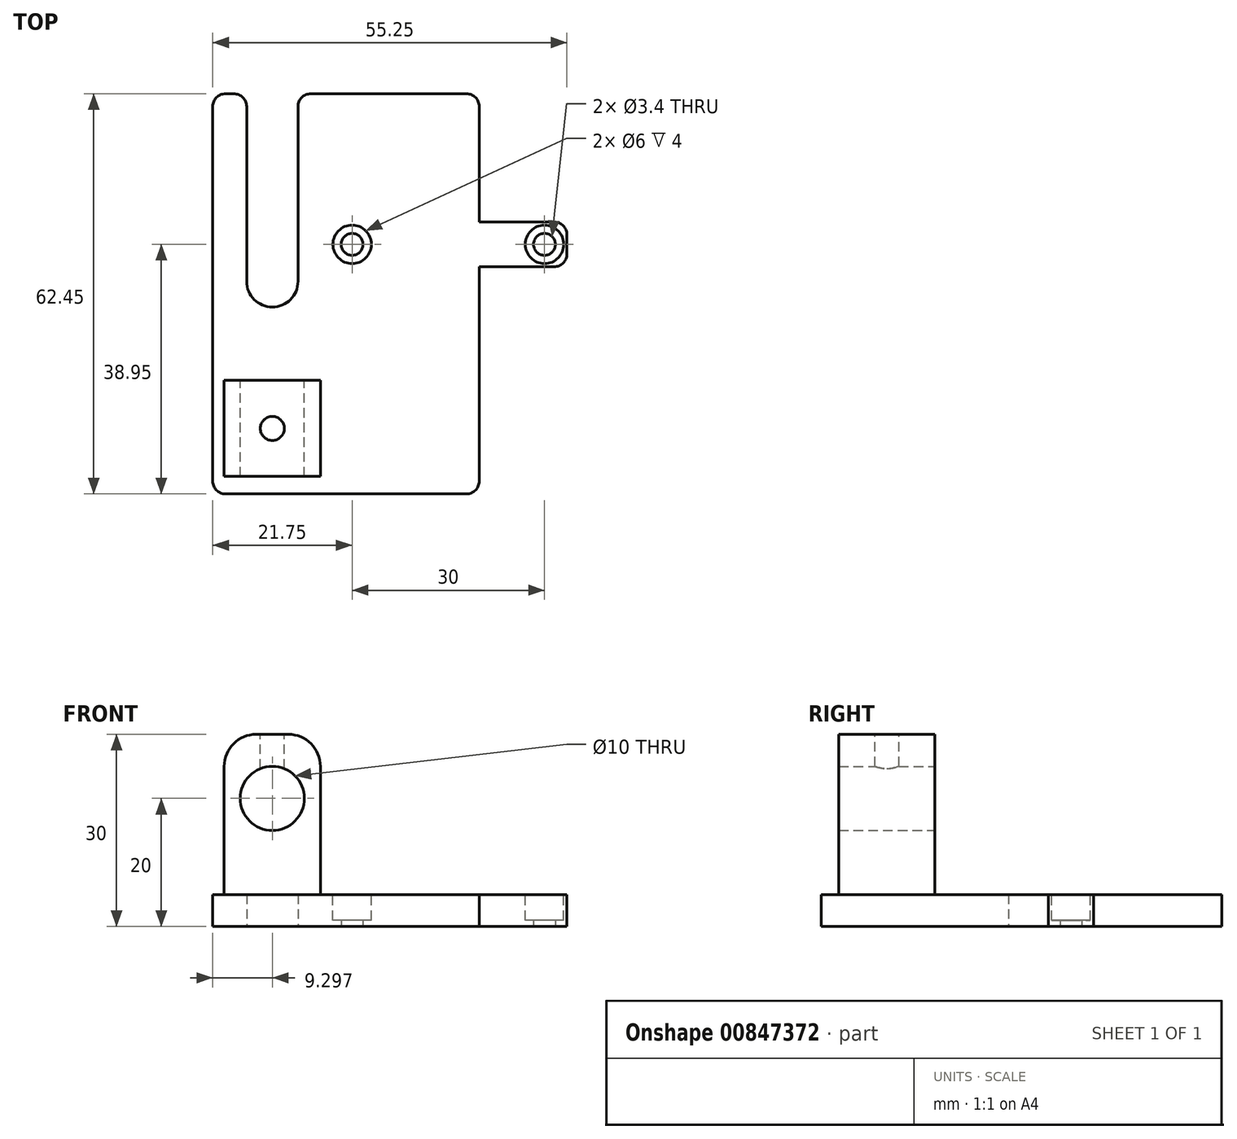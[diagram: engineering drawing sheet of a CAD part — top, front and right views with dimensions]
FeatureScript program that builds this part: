
annotation { "Feature Type Name" : "Feature", "Feature Type Description" : "" }
export const myFeature = defineFeature(function(context is Context, id is Id, definition is map)
    precondition{}
    {
        {
            var Q0;
            Q0=qCreatedBy(makeId("Top.planeOp"),FACE);
            var sketch = newSketch(context, id + "F0", { "sketchPlane" : qUnion([Q0])});
            skLineSegment(sketch, "E0.bottom", {"start": v(0, 0) * mm, "end": v(37, 0) * mm});
            skLineSegment(sketch, "E0.top", {"start": v(0, -7) * mm, "end": v(37, -7) * mm});
            skLineSegment(sketch, "E0.left", {"start": v(0, 0) * mm, "end": v(0, -7) * mm});
            skLineSegment(sketch, "E0.right", {"start": v(37, 0) * mm, "end": v(37, -7) * mm});
            skCircle(sketch, "E1", {"center": v(33.5, -3.5) * mm, "radius": 1.7 * mm});
            skCircle(sketch, "E2", {"center": v(3.5, -3.5) * mm, "radius": 1.7 * mm});
            skLineSegment(sketch, "E3", {"start": v(3.5, -5.2) * mm, "end": v(3.5, -7) * mm, "construction": true});
            skLineSegment(sketch, "E4", {"start": v(1.8, -3.5) * mm, "end": v(0, -3.5) * mm, "construction": true});
            skLineSegment(sketch, "E5", {"start": v(3.5, -1.8) * mm, "end": v(3.5, 0) * mm, "construction": true});
            skLineSegment(sketch, "E6", {"start": v(35.2, -3.5) * mm, "end": v(37, -3.5) * mm, "construction": true});
            skLineSegment(sketch, "E7", {"start": v(33.5, -5.2) * mm, "end": v(33.5, -7) * mm, "construction": true});
            skLineSegment(sketch, "E8", {"start": v(33.5, -1.8) * mm, "end": v(33.5, 0) * mm, "construction": true});
            skLineSegment(sketch, "E9", {"start": v(0, -7) * mm, "end": v(0, -42.45) * mm});
            skLineSegment(sketch, "E10", {"start": v(0, -42.45) * mm, "end": v(23.32, -42.45) * mm});
            skLineSegment(sketch, "E11", {"start": v(23.32, -42.45) * mm, "end": v(23.32, -7) * mm});
            skLineSegment(sketch, "E12", {"start": v(23.32, -7) * mm, "end": v(37, -7) * mm, "construction": true});
            skLineSegment(sketch, "E13", {"start": v(0, 0) * mm, "end": v(0, 20) * mm});
            skLineSegment(sketch, "E14", {"start": v(0, 20) * mm, "end": v(23.32, 20) * mm});
            skLineSegment(sketch, "E15", {"start": v(23.32, 20) * mm, "end": v(23.32, 0) * mm});
            skPoint(sketch, "E16", {"position": v(0, 10) * mm});
            skArc(sketch, "E17", {"start": v(-12.95, -9.28) * mm, "mid": v(-8.95, -13.28) * mm, "end": v(-4.95, -9.28) * mm});
            skLineSegment(sketch, "E18", {"start": v(-12.95, -9.28) * mm, "end": v(-4.95, -9.28) * mm, "construction": true});
            skLineSegment(sketch, "E19", {"start": v(-12.95, 20) * mm, "end": v(-4.95, 20) * mm, "construction": true});
            skLineSegment(sketch, "E20", {"start": v(-12.95, 20) * mm, "end": v(-12.95, -9.28) * mm});
            skLineSegment(sketch, "E21", {"start": v(-4.95, 20) * mm, "end": v(-4.95, -9.28) * mm});
            skLineSegment(sketch, "E22", {"start": v(-12.95, -9.28) * mm, "end": v(0, -9.28) * mm, "construction": true});
            skLineSegment(sketch, "E23", {"start": v(0, -42.45) * mm, "end": v(23.69, -42.45) * mm});
            skLineSegment(sketch, "E24", {"start": v(0, 20) * mm, "end": v(23.69, 20) * mm, "construction": true});
            skLineSegment(sketch, "E25", {"start": v(0, -42.45) * mm, "end": v(23.69, -42.45) * mm, "construction": true});
            skPoint(sketch, "E26", {"position": v(11.66, 20) * mm});
            skLineSegment(sketch, "E27", {"start": v(-8.95, -9.95) * mm, "end": v(-8.95, -13.28) * mm, "construction": true});
            skLineSegment(sketch, "E28", {"start": v(-4.95, 20) * mm, "end": v(0, 20) * mm});
            skLineSegment(sketch, "E29", {"start": v(-12.95, 20) * mm, "end": v(-18.25, 20) * mm});
            skLineSegment(sketch, "E30", {"start": v(-18.25, 20) * mm, "end": v(-18.25, -42.45) * mm});
            skLineSegment(sketch, "E31", {"start": v(-18.25, -42.45) * mm, "end": v(0, -42.45) * mm});
            skSolve(sketch);
        }
        {
            var Q0;
            Q0=makeQuery(id+"F0.imprint","IMPRINT",FACE,{"disambiguationData":[TD([[makeQuery(id+"F0.imprint","IMPRINT",EDGE,{"derivedFrom":sQuery(id+"F0.wireOp",EDGE,"E0.bottom")}),-1.0]])]});
            var Q1;
            {var subQ0=sQuery(id+"F0.wireOp",EDGE,"E9");Q1=makeQuery(id+"F0.imprint","IMPRINT",FACE,{"disambiguationData":[TD([[makeQuery(id+"F0.imprint","IMPRINT",EDGE,{"derivedFrom":subQ0}),1.0]])]});}
            var Q2;
            {var subQ1=sQuery(id+"F0.wireOp",EDGE,"E13");Q2=makeQuery(id+"F0.imprint","IMPRINT",FACE,{"disambiguationData":[TD([[makeQuery(id+"F0.imprint","IMPRINT",EDGE,{"derivedFrom":subQ1}),-1.0]])]});}
            var Q3;
            Q3=makeQuery(id+"F0.imprint","IMPRINT",FACE,{"disambiguationData":[TD([[makeQuery(id+"F0.imprint","IMPRINT",EDGE,{"derivedFrom":sQuery(id+"F0.wireOp",EDGE,"E0.left")}),-1.0]])]});
            extrude(context, id + "F1", {"entities" : qUnion([Q0, Q1, Q2, Q3]), "depth" : 5 * mm, "offsetDistance" : 25 * mm});
        }
        {
            var Q0;
            Q0=makeQuery(id+"F1.opExtrude","CAP_FACE",FACE,{"disambiguationData":[OSD([sQuery(id+"F0.wireOp",EDGE,"E0.bottom"),sQuery(id+"F0.wireOp",EDGE,"E0.top"),sQuery(id+"F0.wireOp",EDGE,"E0.left"),sQuery(id+"F0.wireOp",EDGE,"E0.right"),sQuery(id+"F0.wireOp",EDGE,"E1"),sQuery(id+"F0.wireOp",EDGE,"E2"),sQuery(id+"F0.wireOp",EDGE,"E9"),sQuery(id+"F0.wireOp",EDGE,"E10"),sQuery(id+"F0.wireOp",EDGE,"E11"),sQuery(id+"F0.wireOp",EDGE,"E13"),sQuery(id+"F0.wireOp",EDGE,"E14"),sQuery(id+"F0.wireOp",EDGE,"E15"),sQuery(id+"F0.wireOp",EDGE,"E17"),sQuery(id+"F0.wireOp",EDGE,"E20"),sQuery(id+"F0.wireOp",EDGE,"E21"),sQuery(id+"F0.wireOp",EDGE,"E23")])],"isStart":false});
            var sketch = newSketch(context, id + "F2", { "sketchPlane" : qUnion([Q0])});
            skCircle(sketch, "E32", {"center": v(3.5, -3.5) * mm, "radius": 3 * mm});
            skCircle(sketch, "E33", {"center": v(33.5, -3.5) * mm, "radius": 3 * mm});
            skSolve(sketch);
        }
        {
            var Q0;
            Q0=makeQuery(id+"F2.imprint","IMPRINT",FACE,{"disambiguationData":[TD([[makeQuery(id+"F2.imprint","IMPRINT",EDGE,{"derivedFrom":makeQuery(id+"F1.opExtrude","CAP_EDGE",EDGE,{"disambiguationData":[OSD([sQuery(id+"F0.wireOp",EDGE,"E2")])],"isStart":false})}),-1.0]])]});
            var Q1;
            Q1=makeQuery(id+"F2.imprint","IMPRINT",FACE,{"disambiguationData":[TD([[makeQuery(id+"F2.imprint","IMPRINT",EDGE,{"derivedFrom":makeQuery(id+"F1.opExtrude","CAP_EDGE",EDGE,{"disambiguationData":[OSD([sQuery(id+"F0.wireOp",EDGE,"E1")])],"isStart":false})}),-1.0]])]});
            extrude(context, id + "F3", {"entities" : qUnion([Q0, Q1]), "operationType" : NewBodyOperationType.REMOVE, "oppositeDirection" : true, "depth" : 4 * mm, "offsetDistance" : 25 * mm});
        }
        {
            var Q0;
            Q0=makeQuery(id+"F1.opExtrude","CAP_FACE",FACE,{"disambiguationData":[OSD([sQuery(id+"F0.wireOp",EDGE,"E0.bottom"),sQuery(id+"F0.wireOp",EDGE,"E0.top"),sQuery(id+"F0.wireOp",EDGE,"E0.left"),sQuery(id+"F0.wireOp",EDGE,"E0.right"),sQuery(id+"F0.wireOp",EDGE,"E1"),sQuery(id+"F0.wireOp",EDGE,"E2"),sQuery(id+"F0.wireOp",EDGE,"E9"),sQuery(id+"F0.wireOp",EDGE,"E13"),sQuery(id+"F0.wireOp",EDGE,"E14"),sQuery(id+"F0.wireOp",EDGE,"GDynNiDg-9xj2-320R-Va1n-F43uqJFQxb5q"),sQuery(id+"F0.wireOp",EDGE,"E17"),sQuery(id+"F0.wireOp",EDGE,"E20"),sQuery(id+"F0.wireOp",EDGE,"E21"),sQuery(id+"F0.wireOp",EDGE,"RT2sn7US-NrVC-GBVw-aXR2-7VAFfpac8IiJ"),sQuery(id+"F0.wireOp",EDGE,"Kn5Iz3uP-NdwH-uD1Z-zRby-fDGWd2xC9ESL"),sQuery(id+"F0.wireOp",EDGE,"E23")])],"isStart":false});
            var sketch = newSketch(context, id + "F4", { "sketchPlane" : qUnion([Q0])});
            skLineSegment(sketch, "E34.bottom", {"start": v(-16.45, -24.72) * mm, "end": v(-1.45, -24.72) * mm});
            skLineSegment(sketch, "E34.top", {"start": v(-16.45, -39.72) * mm, "end": v(-1.45, -39.72) * mm});
            skLineSegment(sketch, "E34.left", {"start": v(-16.45, -24.72) * mm, "end": v(-16.45, -39.72) * mm});
            skLineSegment(sketch, "E34.right", {"start": v(-1.45, -24.72) * mm, "end": v(-1.45, -39.72) * mm});
            skLineSegment(sketch, "E35", {"start": v(-16.45, -24.72) * mm, "end": v(-8.95, -24.72) * mm, "construction": true});
            skLineSegment(sketch, "E36", {"start": v(-1.45, -24.72) * mm, "end": v(-8.95, -24.72) * mm, "construction": true});
            skSolve(sketch);
        }
        {
            var Q0;
            Q0=makeQuery(id+"F4.imprint","IMPRINT",FACE,{"disambiguationData":[TD([[makeQuery(id+"F4.imprint","IMPRINT",EDGE,{"derivedFrom":sQuery(id+"F4.wireOp",EDGE,"E34.bottom")}),-1.0]])]});
            extrude(context, id + "F5", {"entities" : qUnion([Q0]), "operationType" : NewBodyOperationType.ADD, "depth" : 25 * mm, "offsetDistance" : 25 * mm});
        }
        {
            var Q0;
            Q0=makeQuery(id+"F5.opExtrude","SWEPT_FACE",FACE,{"disambiguationData":[OSD([sQuery(id+"F4.wireOp",EDGE,"E34.bottom")])]});
            var sketch = newSketch(context, id + "F6", { "sketchPlane" : qUnion([Q0])});
            skCircle(sketch, "E37", {"center": v(8.95, 20) * mm, "radius": 5 * mm});
            skLineSegment(sketch, "E38", {"start": v(8.95, 20) * mm, "end": v(1.45, 20) * mm, "construction": true});
            skLineSegment(sketch, "E39", {"start": v(8.95, 20) * mm, "end": v(16.45, 20) * mm, "construction": true});
            skSolve(sketch);
        }
        {
            var Q0;
            Q0=makeQuery(id+"F6.imprint","IMPRINT",FACE,{"disambiguationData":[TD([[makeQuery(id+"F6.imprint","IMPRINT",EDGE,{"derivedFrom":sQuery(id+"F6.wireOp",EDGE,"E37")}),1.0]])]});
            extrude(context, id + "F7", {"entities" : qUnion([Q0]), "operationType" : NewBodyOperationType.REMOVE, "oppositeDirection" : true, "depth" : 15 * mm, "offsetDistance" : 25 * mm});
        }
        {
            var Q0;
            Q0=makeQuery(id+"F1.opExtrude","SWEPT_EDGE",EDGE,{"disambiguationData":[OSD([sQuery(id+"F0.wireOp",EDGE,"E14"),sQuery(id+"F0.wireOp",EDGE,"E15")])]});
            var Q1;
            Q1=makeQuery(id+"F1.opExtrude","SWEPT_EDGE",EDGE,{"disambiguationData":[OSD([sQuery(id+"F0.wireOp",EDGE,"E14"),sQuery(id+"F0.wireOp",EDGE,"E21")])]});
            var Q2;
            Q2=makeQuery(id+"F1.opExtrude","SWEPT_EDGE",EDGE,{"disambiguationData":[OSD([sQuery(id+"F0.wireOp",EDGE,"E14"),sQuery(id+"F0.wireOp",EDGE,"E20")])]});
            var Q3;
            Q3=makeQuery(id+"F1.opExtrude","SWEPT_EDGE",EDGE,{"disambiguationData":[OSD([sQuery(id+"F0.wireOp",EDGE,"E13"),sQuery(id+"F0.wireOp",EDGE,"E14")])]});
            var Q4;
            Q4=makeQuery(id+"F1.opExtrude","SWEPT_EDGE",EDGE,{"disambiguationData":[OSD([sQuery(id+"F0.wireOp",EDGE,"E0.bottom"),sQuery(id+"F0.wireOp",EDGE,"E0.right")])]});
            var Q5;
            Q5=makeQuery(id+"F1.opExtrude","SWEPT_EDGE",EDGE,{"disambiguationData":[OSD([sQuery(id+"F0.wireOp",EDGE,"E0.top"),sQuery(id+"F0.wireOp",EDGE,"E0.right")])]});
            var Q6;
            Q6=makeQuery(id+"F1.opExtrude","SWEPT_EDGE",EDGE,{"disambiguationData":[OSD([sQuery(id+"F0.wireOp",EDGE,"E10"),sQuery(id+"F0.wireOp",EDGE,"E11")])]});
            var Q7;
            Q7=makeQuery(id+"F1.opExtrude","SWEPT_EDGE",EDGE,{"disambiguationData":[OSD([sQuery(id+"F0.wireOp",EDGE,"E29"),sQuery(id+"F0.wireOp",EDGE,"E30")])]});
            var Q8;
            Q8=makeQuery(id+"F1.opExtrude","SWEPT_EDGE",EDGE,{"disambiguationData":[OSD([sQuery(id+"F0.wireOp",EDGE,"E30"),sQuery(id+"F0.wireOp",EDGE,"E31")])]});
            fillet(context, id + "F8", {"entities" : qUnion([Q0, Q1, Q2, Q3, Q4, Q5, Q6, Q7, Q8]), "radius" : 2 * mm, "tangentPropagation" : true, "allowEdgeOverflow" : false});
        }
        {
            var Q0;
            Q0=makeQuery(id+"F5.opExtrude","CAP_FACE",FACE,{"disambiguationData":[OSD([sQuery(id+"F4.wireOp",EDGE,"E34.bottom"),sQuery(id+"F4.wireOp",EDGE,"E34.top"),sQuery(id+"F4.wireOp",EDGE,"E34.left"),sQuery(id+"F4.wireOp",EDGE,"E34.right")])],"isStart":false});
            var sketch = newSketch(context, id + "F9", { "sketchPlane" : qUnion([Q0])});
            skCircle(sketch, "E40", {"center": v(-8.95, -32.22) * mm, "radius": 1.87 * mm});
            skLineSegment(sketch, "E41", {"start": v(-16.45, -32.22) * mm, "end": v(-8.95, -32.22) * mm, "construction": true});
            skLineSegment(sketch, "E42", {"start": v(-8.95, -32.22) * mm, "end": v(-1.45, -32.22) * mm, "construction": true});
            skSolve(sketch);
        }
        {
            var Q0;
            Q0=makeQuery(id+"F9.imprint","IMPRINT",FACE,{"disambiguationData":[TD([[makeQuery(id+"F9.imprint","IMPRINT",EDGE,{"derivedFrom":sQuery(id+"F9.wireOp",EDGE,"E40")}),1.0]])]});
            extrude(context, id + "F10", {"entities" : qUnion([Q0]), "operationType" : NewBodyOperationType.REMOVE, "oppositeDirection" : true, "depth" : 7 * mm, "offsetDistance" : 25 * mm});
        }
        {
            var Q0;
            Q0=makeQuery(id+"F5.opExtrude","CAP_EDGE",EDGE,{"disambiguationData":[OSD([sQuery(id+"F4.wireOp",EDGE,"E34.right")])],"isStart":false});
            var Q1;
            Q1=makeQuery(id+"F5.opExtrude","CAP_EDGE",EDGE,{"disambiguationData":[OSD([sQuery(id+"F4.wireOp",EDGE,"E34.left")])],"isStart":false});
            fillet(context, id + "F11", {"entities" : qUnion([Q0, Q1]), "radius" : 5 * mm, "tangentPropagation" : true, "allowEdgeOverflow" : false});
        }
    });
